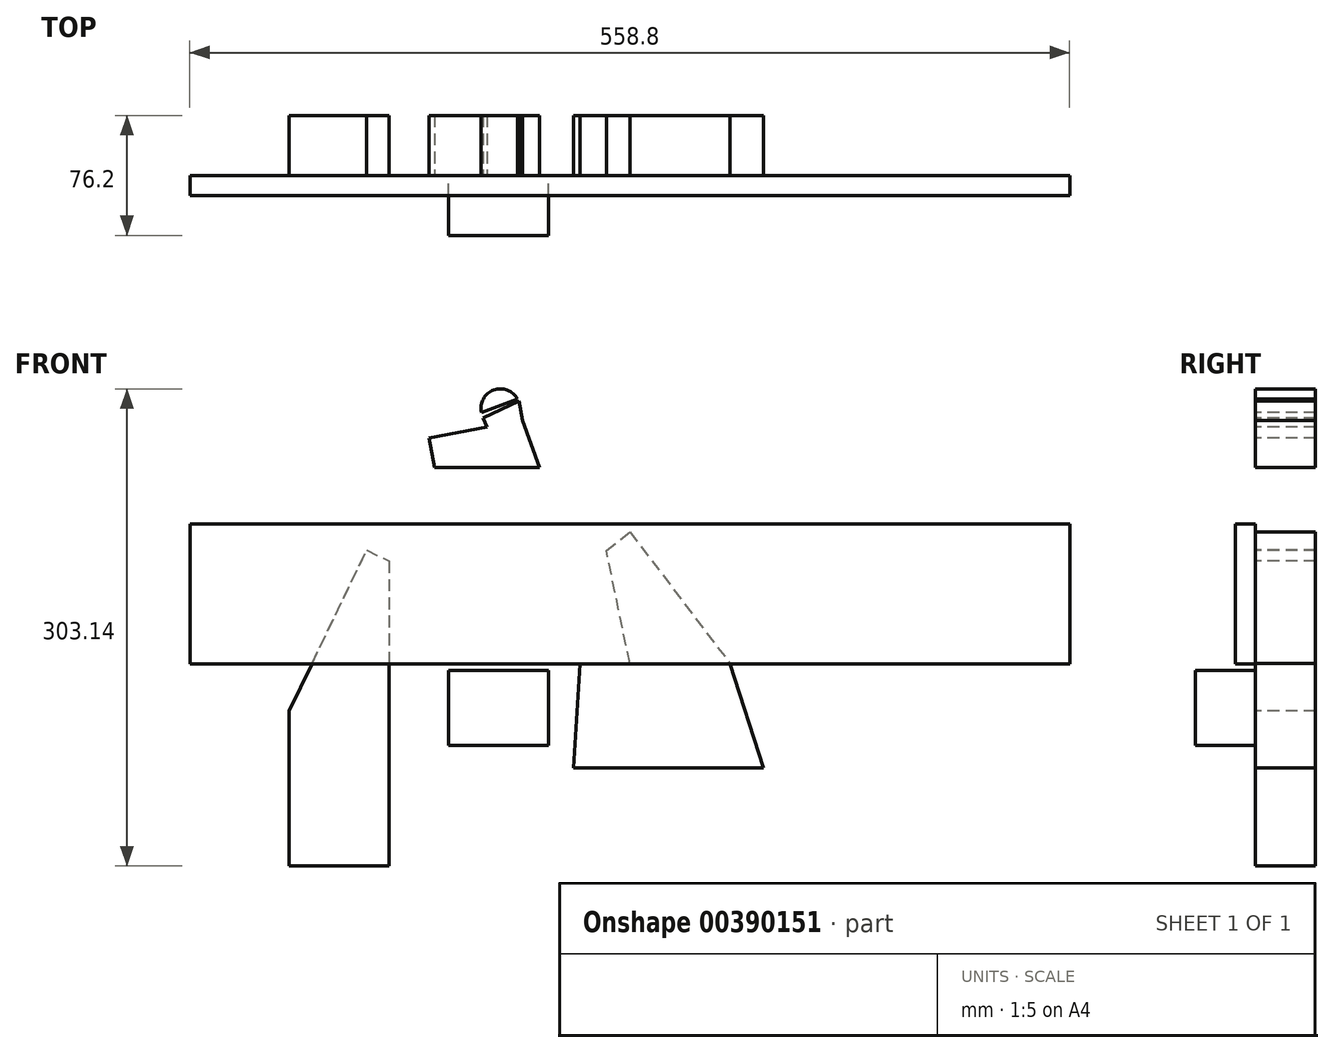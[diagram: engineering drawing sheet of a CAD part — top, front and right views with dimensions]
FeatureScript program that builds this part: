
annotation { "Feature Type Name" : "Feature", "Feature Type Description" : "" }
export const myFeature = defineFeature(function(context is Context, id is Id, definition is map)
    precondition{}
    {
        {
            var Q0;
            Q0=qCreatedBy(makeId("Front.planeOp"),FACE);
            var sketch = newSketch(context, id + "F0", { "sketchPlane" : qUnion([Q0])});
            skLineSegment(sketch, "E0", {"start": v(-14.91, 33.68) * mm, "end": v(0, 45.54) * mm});
            skLineSegment(sketch, "E1", {"start": v(0, 45.54) * mm, "end": v(63.5, -37.8) * mm});
            skLineSegment(sketch, "E2", {"start": v(63.5, -37.8) * mm, "end": v(0, -37.8) * mm});
            skLineSegment(sketch, "E3", {"start": v(0, -37.8) * mm, "end": v(-14.91, 33.68) * mm});
            skLineSegment(sketch, "E4", {"start": v(-31.75, -37.8) * mm, "end": v(63.5, -37.8) * mm});
            skLineSegment(sketch, "E5", {"start": v(84.73, -104.35) * mm, "end": v(63.5, -37.8) * mm});
            skLineSegment(sketch, "E6", {"start": v(-35.92, -104.35) * mm, "end": v(84.73, -104.35) * mm});
            skLineSegment(sketch, "E7", {"start": v(-31.75, -37.8) * mm, "end": v(-35.92, -104.35) * mm});
            skSolve(sketch);
        }
        {
            var Q0;
            Q0=makeQuery(id+"F0.imprint","IMPRINT",FACE,{"disambiguationData":[TD([[makeQuery(id+"F0.imprint","IMPRINT",EDGE,{"derivedFrom":sQuery(id+"F0.wireOp",EDGE,"E0")}),-1.0]])]});
            var Q1;
            {var subQ0=sQuery(id+"F0.wireOp",EDGE,"E5");Q1=makeQuery(id+"F0.imprint","IMPRINT",FACE,{"disambiguationData":[TD([[makeQuery(id+"F0.imprint","IMPRINT",EDGE,{"derivedFrom":subQ0}),1.0]])]});}
            extrude(context, id + "F1", {"entities" : qUnion([Q0, Q1]), "oppositeDirection" : true, "depth" : 38.1 * mm});
        }
        {
            var Q0;
            Q0=qCreatedBy(makeId("Front.planeOp"),FACE);
            var sketch = newSketch(context, id + "F2", { "sketchPlane" : qUnion([Q0])});
            skLineSegment(sketch, "E8", {"start": v(-167.14, 34.02) * mm, "end": v(-152.9, 27) * mm});
            skLineSegment(sketch, "E9", {"start": v(-152.9, 27) * mm, "end": v(-152.9, -166.68) * mm});
            skLineSegment(sketch, "E10", {"start": v(-152.9, -166.68) * mm, "end": v(-216.4, -166.68) * mm});
            skLineSegment(sketch, "E11", {"start": v(-216.4, -166.68) * mm, "end": v(-216.4, -68.25) * mm});
            skLineSegment(sketch, "E12", {"start": v(-216.4, -68.25) * mm, "end": v(-167.14, 34.02) * mm});
            skSolve(sketch);
        }
        {
            var Q0;
            Q0=makeQuery(id+"F2.imprint","IMPRINT",FACE,{"disambiguationData":[TD([[makeQuery(id+"F2.imprint","IMPRINT",EDGE,{"derivedFrom":sQuery(id+"F2.wireOp",EDGE,"E8")}),-1.0]])]});
            extrude(context, id + "F3", {"entities" : qUnion([Q0]), "oppositeDirection" : true, "depth" : 38.1 * mm});
        }
        {
            var Q0;
            Q0=qCreatedBy(makeId("Front.planeOp"),FACE);
            var sketch = newSketch(context, id + "F4", { "sketchPlane" : qUnion([Q0])});
            skLineSegment(sketch, "E13", {"start": v(-127.42, 105.23) * mm, "end": v(-123.91, 86.5) * mm});
            skLineSegment(sketch, "E14", {"start": v(-123.91, 86.5) * mm, "end": v(-57.24, 86.5) * mm});
            skLineSegment(sketch, "E15", {"start": v(-57.24, 86.5) * mm, "end": v(-68.12, 116.33) * mm});
            skLineSegment(sketch, "E16", {"start": v(-68.12, 116.33) * mm, "end": v(-127.42, 105.23) * mm});
            skPoint(sketch, "E17.start.orphan", {"position": v(-68.12, 129.47) * mm});
            skLineSegment(sketch, "E18", {"start": v(-68.12, 116.33) * mm, "end": v(-70.46, 128.8) * mm});
            skLineSegment(sketch, "E19", {"start": v(-70.46, 128.8) * mm, "end": v(-93.37, 117.84) * mm});
            skLineSegment(sketch, "E20", {"start": v(-93.37, 117.84) * mm, "end": v(-90.63, 112.11) * mm});
            skLineSegment(sketch, "E21", {"start": v(-90.63, 112.11) * mm, "end": v(-68.12, 116.33) * mm});
            skSolve(sketch);
        }
        {
            var Q0;
            {var subQ3=sQuery(id+"F4.wireOp",EDGE,"E13");Q0=makeQuery(id+"F4.imprint","IMPRINT",FACE,{"disambiguationData":[TD([[makeQuery(id+"F4.imprint","IMPRINT",EDGE,{"derivedFrom":subQ3}),1.0]])]});}
            var Q1;
            {var subQ0=sQuery(id+"F4.wireOp",EDGE,"E18");Q1=makeQuery(id+"F4.imprint","IMPRINT",FACE,{"disambiguationData":[TD([[makeQuery(id+"F4.imprint","IMPRINT",EDGE,{"derivedFrom":subQ0}),1.0]])]});}
            extrude(context, id + "F5", {"entities" : qUnion([Q0, Q1]), "oppositeDirection" : true, "depth" : 38.1 * mm});
        }
        {
            var Q0;
            Q0=qCreatedBy(makeId("Front.planeOp"),FACE);
            var sketch = newSketch(context, id + "F6", { "sketchPlane" : qUnion([Q0])});
            skLineSegment(sketch, "E22.bottom", {"start": v(-115.11, -42.4) * mm, "end": v(-51.61, -42.4) * mm});
            skLineSegment(sketch, "E22.top", {"start": v(-115.11, -90.03) * mm, "end": v(-51.61, -90.03) * mm});
            skLineSegment(sketch, "E22.left", {"start": v(-115.11, -42.4) * mm, "end": v(-115.11, -90.03) * mm});
            skLineSegment(sketch, "E22.right", {"start": v(-51.61, -42.4) * mm, "end": v(-51.61, -90.03) * mm});
            skSolve(sketch);
        }
        {
            var Q0;
            Q0=makeQuery(id+"F6.imprint","IMPRINT",FACE,{"disambiguationData":[TD([[makeQuery(id+"F6.imprint","IMPRINT",EDGE,{"derivedFrom":sQuery(id+"F6.wireOp",EDGE,"E22.bottom")}),-1.0]])]});
            extrude(context, id + "F7", {"entities" : qUnion([Q0]), "depth" : 38.1 * mm});
        }
        {
            var Q0;
            Q0=qCreatedBy(makeId("Front.planeOp"),FACE);
            var sketch = newSketch(context, id + "F8", { "sketchPlane" : qUnion([Q0])});
            skArc(sketch, "E23", {"start": v(-71.4, 129.93) * mm, "mid": v(-86.5, 135.71) * mm, "end": v(-94.29, 121.56) * mm});
            skLineSegment(sketch, "E24", {"start": v(-94.29, 121.56) * mm, "end": v(-71.4, 129.93) * mm});
            skSolve(sketch);
        }
        {
            var Q0;
            Q0 = qSketchRegion(id + "F8", true);
            extrude(context, id + "F9", {"entities" : qUnion([Q0]), "oppositeDirection" : true, "depth" : 38.1 * mm});
        }
        {
            var Q0;
            Q0=qCreatedBy(makeId("Front.planeOp"),FACE);
            var sketch = newSketch(context, id + "F10", { "sketchPlane" : qUnion([Q0])});
            skLineSegment(sketch, "E25.bottom", {"start": v(-281.02, 221.44) * mm, "end": v(277.78, 221.44) * mm});
            skLineSegment(sketch, "E25.top", {"start": v(-281.02, -172.26) * mm, "end": v(277.78, -172.26) * mm});
            skLineSegment(sketch, "E25.left", {"start": v(-281.02, 221.44) * mm, "end": v(-281.02, -172.26) * mm});
            skLineSegment(sketch, "E25.right", {"start": v(277.78, 221.44) * mm, "end": v(277.78, -172.26) * mm});
            skSolve(sketch);
        }
        {
            var Q0;
            Q0=qCreatedBy(makeId("Front.planeOp"),FACE);
            var sketch = newSketch(context, id + "F11", { "sketchPlane" : qUnion([Q0])});
            skLineSegment(sketch, "E26.bottom", {"start": v(279.34, -38.15) * mm, "end": v(-279.46, -38.15) * mm});
            skLineSegment(sketch, "E26.top", {"start": v(279.34, 50.75) * mm, "end": v(-279.46, 50.75) * mm});
            skLineSegment(sketch, "E26.left", {"start": v(279.34, -38.15) * mm, "end": v(279.34, 50.75) * mm});
            skLineSegment(sketch, "E26.right", {"start": v(-279.46, -38.15) * mm, "end": v(-279.46, 50.75) * mm});
            skPoint(sketch, "E26.middle", {"position": v(-0.06, 6.3) * mm});
            skSolve(sketch);
        }
        {
            var Q0;
            Q0=makeQuery(id+"F11.imprint","IMPRINT",FACE,{"disambiguationData":[TD([[makeQuery(id+"F11.imprint","IMPRINT",EDGE,{"derivedFrom":sQuery(id+"F11.wireOp",EDGE,"E26.bottom")}),-1.0]])]});
            extrude(context, id + "F12", {"entities" : qUnion([Q0]), "depth" : 12.7 * mm});
        }
    });
